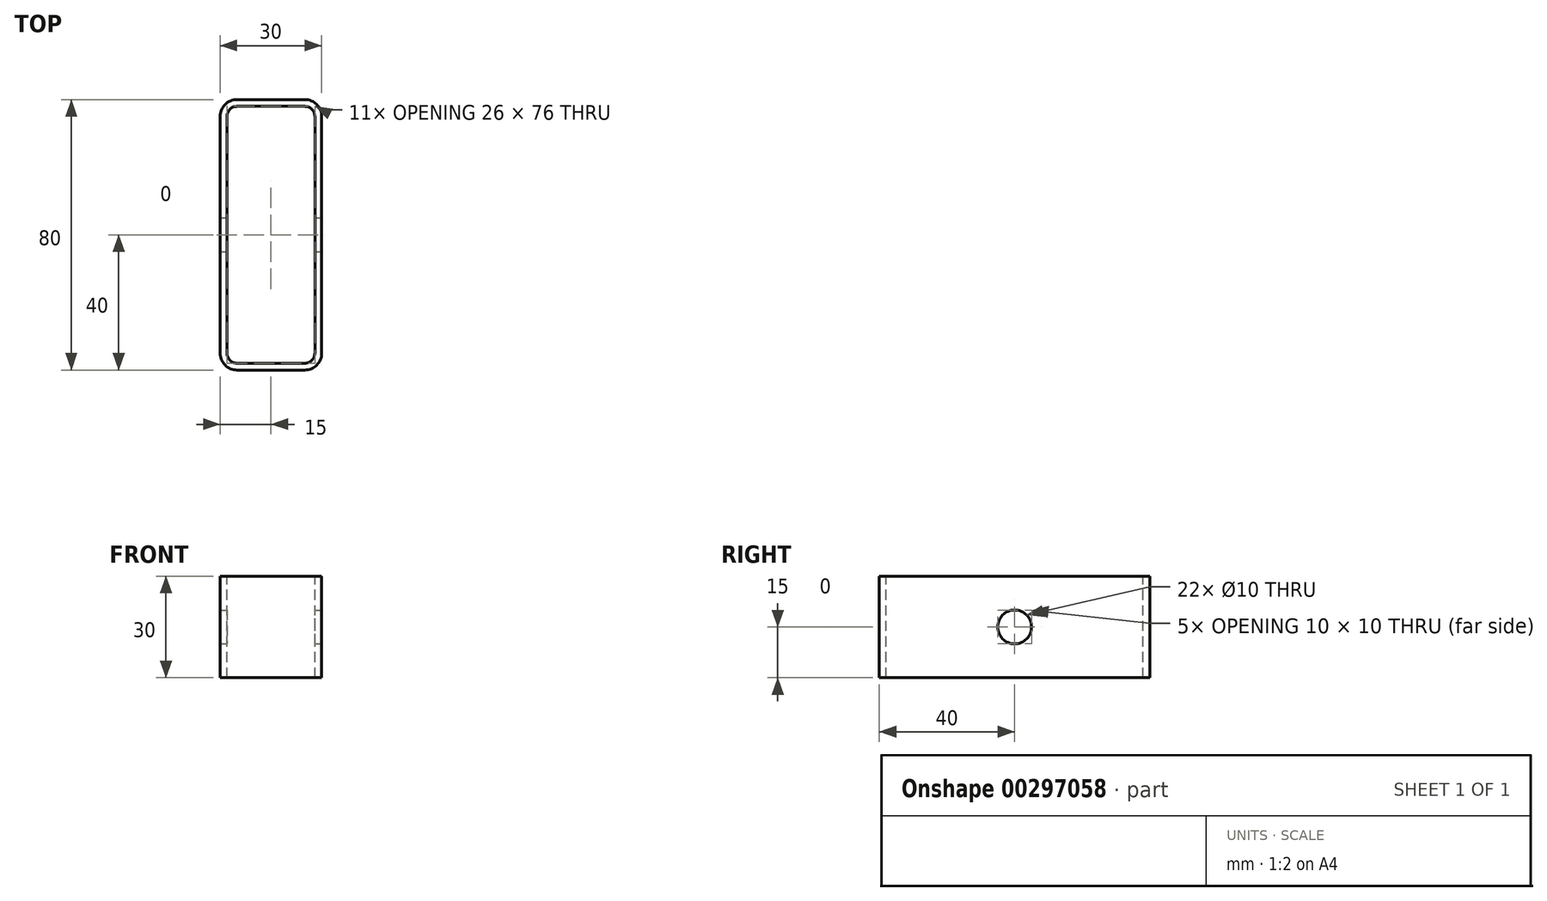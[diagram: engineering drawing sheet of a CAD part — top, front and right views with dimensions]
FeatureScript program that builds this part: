
annotation { "Feature Type Name" : "Feature", "Feature Type Description" : "" }
export const myFeature = defineFeature(function(context is Context, id is Id, definition is map)
    precondition{}
    {
        {
            var Q0;
            Q0=qCreatedBy(makeId("Top.planeOp"),FACE);
            var sketch = newSketch(context, id + "F0", { "sketchPlane" : qUnion([Q0])});
            skLineSegment(sketch, "E0.bottom", {"start": v(15, 40) * mm, "end": v(-15, 40) * mm});
            skLineSegment(sketch, "E0.top", {"start": v(15, -40) * mm, "end": v(-15, -40) * mm});
            skLineSegment(sketch, "E0.left", {"start": v(15, 40) * mm, "end": v(15, -40) * mm});
            skLineSegment(sketch, "E0.right", {"start": v(-15, 40) * mm, "end": v(-15, -40) * mm});
            skPoint(sketch, "E0.middle", {"position": v(0, 0) * mm});
            skSolve(sketch);
        }
        {
            var Q0;
            Q0=makeQuery(id+"F0.imprint","IMPRINT",FACE,{"disambiguationData":[TD([[makeQuery(id+"F0.imprint","IMPRINT",EDGE,{"derivedFrom":sQuery(id+"F0.wireOp",EDGE,"E0.bottom")}),1.0]])]});
            extrude(context, id + "F1", {"entities" : qUnion([Q0]), "depth" : 30 * mm});
        }
        {
            var Q0;
            Q0=makeQuery(id+"F1.opExtrude","SWEPT_EDGE",EDGE,{"disambiguationData":[OSD([sQuery(id+"F0.wireOp",EDGE,"E0.bottom"),sQuery(id+"F0.wireOp",EDGE,"E0.left")])]});
            var Q1;
            Q1=makeQuery(id+"F1.opExtrude","SWEPT_EDGE",EDGE,{"disambiguationData":[OSD([sQuery(id+"F0.wireOp",EDGE,"E0.bottom"),sQuery(id+"F0.wireOp",EDGE,"E0.right")])]});
            var Q2;
            Q2=makeQuery(id+"F1.opExtrude","SWEPT_EDGE",EDGE,{"disambiguationData":[OSD([sQuery(id+"F0.wireOp",EDGE,"E0.top"),sQuery(id+"F0.wireOp",EDGE,"E0.right")])]});
            var Q3;
            Q3=makeQuery(id+"F1.opExtrude","SWEPT_EDGE",EDGE,{"disambiguationData":[OSD([sQuery(id+"F0.wireOp",EDGE,"E0.top"),sQuery(id+"F0.wireOp",EDGE,"E0.left")])]});
            fillet(context, id + "F2", {"entities" : qUnion([Q0, Q1, Q2, Q3]), "radius" : 5 * mm, "tangentPropagation" : true, "allowEdgeOverflow" : false});
        }
        {
            var Q0;
            Q0=makeQuery(id+"F1.opExtrude","CAP_FACE",FACE,{"disambiguationData":[OSD([sQuery(id+"F0.wireOp",EDGE,"E0.bottom"),sQuery(id+"F0.wireOp",EDGE,"E0.top"),sQuery(id+"F0.wireOp",EDGE,"E0.left"),sQuery(id+"F0.wireOp",EDGE,"E0.right")])],"isStart":false});
            var sketch = newSketch(context, id + "F3", { "sketchPlane" : qUnion([Q0])});
            skLineSegment(sketch, "E1.0.0", {"start": v(-10, -40) * mm, "end": v(10, -40) * mm});
            skArc(sketch, "E1.0.1", {"start": v(10, -40) * mm, "mid": v(13.54, -38.54) * mm, "end": v(15, -35) * mm});
            skLineSegment(sketch, "E1.0.2", {"start": v(15, -35) * mm, "end": v(15, 35) * mm});
            skArc(sketch, "E1.0.3", {"start": v(15, 35) * mm, "mid": v(13.54, 38.54) * mm, "end": v(10, 40) * mm});
            skLineSegment(sketch, "E1.0.4", {"start": v(10, 40) * mm, "end": v(-10, 40) * mm});
            skArc(sketch, "E1.0.5", {"start": v(-10, 40) * mm, "mid": v(-13.54, 38.54) * mm, "end": v(-15, 35) * mm});
            skLineSegment(sketch, "E1.0.6", {"start": v(-15, 35) * mm, "end": v(-15, -35) * mm});
            skArc(sketch, "E1.0.7", {"start": v(-15, -35) * mm, "mid": v(-13.54, -38.54) * mm, "end": v(-10, -40) * mm});
            skLineSegment(sketch, "E2.0", {"start": v(10, 38) * mm, "end": v(-10, 38) * mm});
            skArc(sketch, "E2.1", {"start": v(13, 35) * mm, "mid": v(12.12, 37.12) * mm, "end": v(10, 38) * mm});
            skArc(sketch, "E2.2", {"start": v(-10, 38) * mm, "mid": v(-12.12, 37.12) * mm, "end": v(-13, 35) * mm});
            skLineSegment(sketch, "E2.3", {"start": v(13, -35) * mm, "end": v(13, 35) * mm});
            skLineSegment(sketch, "E2.4", {"start": v(-13, 35) * mm, "end": v(-13, -35) * mm});
            skArc(sketch, "E2.5", {"start": v(-13, -35) * mm, "mid": v(-12.12, -37.12) * mm, "end": v(-10, -38) * mm});
            skLineSegment(sketch, "E2.6", {"start": v(-10, -38) * mm, "end": v(10, -38) * mm});
            skArc(sketch, "E2.7", {"start": v(10, -38) * mm, "mid": v(12.12, -37.12) * mm, "end": v(13, -35) * mm});
            skSolve(sketch);
        }
        {
            var Q0;
            Q0=makeQuery(id+"F3.imprint","IMPRINT",FACE,{"disambiguationData":[TD([[makeQuery(id+"F3.imprint","IMPRINT",EDGE,{"derivedFrom":sQuery(id+"F3.wireOp",EDGE,"E2.0")}),1.0]])]});
            extrude(context, id + "F4", {"entities" : qUnion([Q0]), "operationType" : NewBodyOperationType.REMOVE, "oppositeDirection" : true, "depth" : 30 * mm});
        }
        {
            var Q0;
            Q0=makeQuery(id+"F1.opExtrude","SWEPT_FACE",FACE,{"disambiguationData":[OSD([sQuery(id+"F0.wireOp",EDGE,"E0.left")])]});
            var sketch = newSketch(context, id + "F5", { "sketchPlane" : qUnion([Q0])});
            skCircle(sketch, "E3", {"center": v(0, 15) * mm, "radius": 5 * mm});
            skPoint(sketch, "E3.centerSnap0", {"position": v(35, 15) * mm});
            skSolve(sketch);
        }
        {
            var Q0;
            Q0=makeQuery(id+"F5.imprint","IMPRINT",FACE,{"disambiguationData":[TD([[makeQuery(id+"F5.imprint","IMPRINT",EDGE,{"derivedFrom":sQuery(id+"F5.wireOp",EDGE,"E3")}),1.0]])]});
            extrude(context, id + "F6", {"entities" : qUnion([Q0]), "operationType" : NewBodyOperationType.REMOVE, "oppositeDirection" : true, "depth" : 30 * mm});
        }
    });
